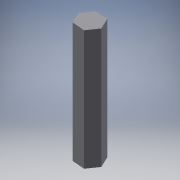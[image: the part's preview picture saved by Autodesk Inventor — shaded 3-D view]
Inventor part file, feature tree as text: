
AUTODESK INVENTOR PART (.ipt)
format: ipt  version: 2017 (Build 210142000, 142)  size: 99,840 bytes
history: native  units: in
note: dims shown in document units (in); Inventor stores cm internally (conversion verified against a paired STEP export)
features: extrude x2, sketch x2
ambient origin geometry x8: Origin, YZ Plane, XZ Plane, XY Plane, X Axis, Y Axis, Z Axis, Center Point
bodies: Solid1 (feature_tree)
feature tree (4):
  extrude  "Extrusion1"  Depth=2.3in TaperAngle=0.0deg
  extrude  "Extrusion2"  Depth=2.8in TaperAngle=0.0deg
  sketch  "Sketch1"  dims[d0=0.5in d1=2.3in d2=0.0in]
  sketch  "Sketch4"  dims[d4=0.25in d5=2.8in d6=0.0in]
